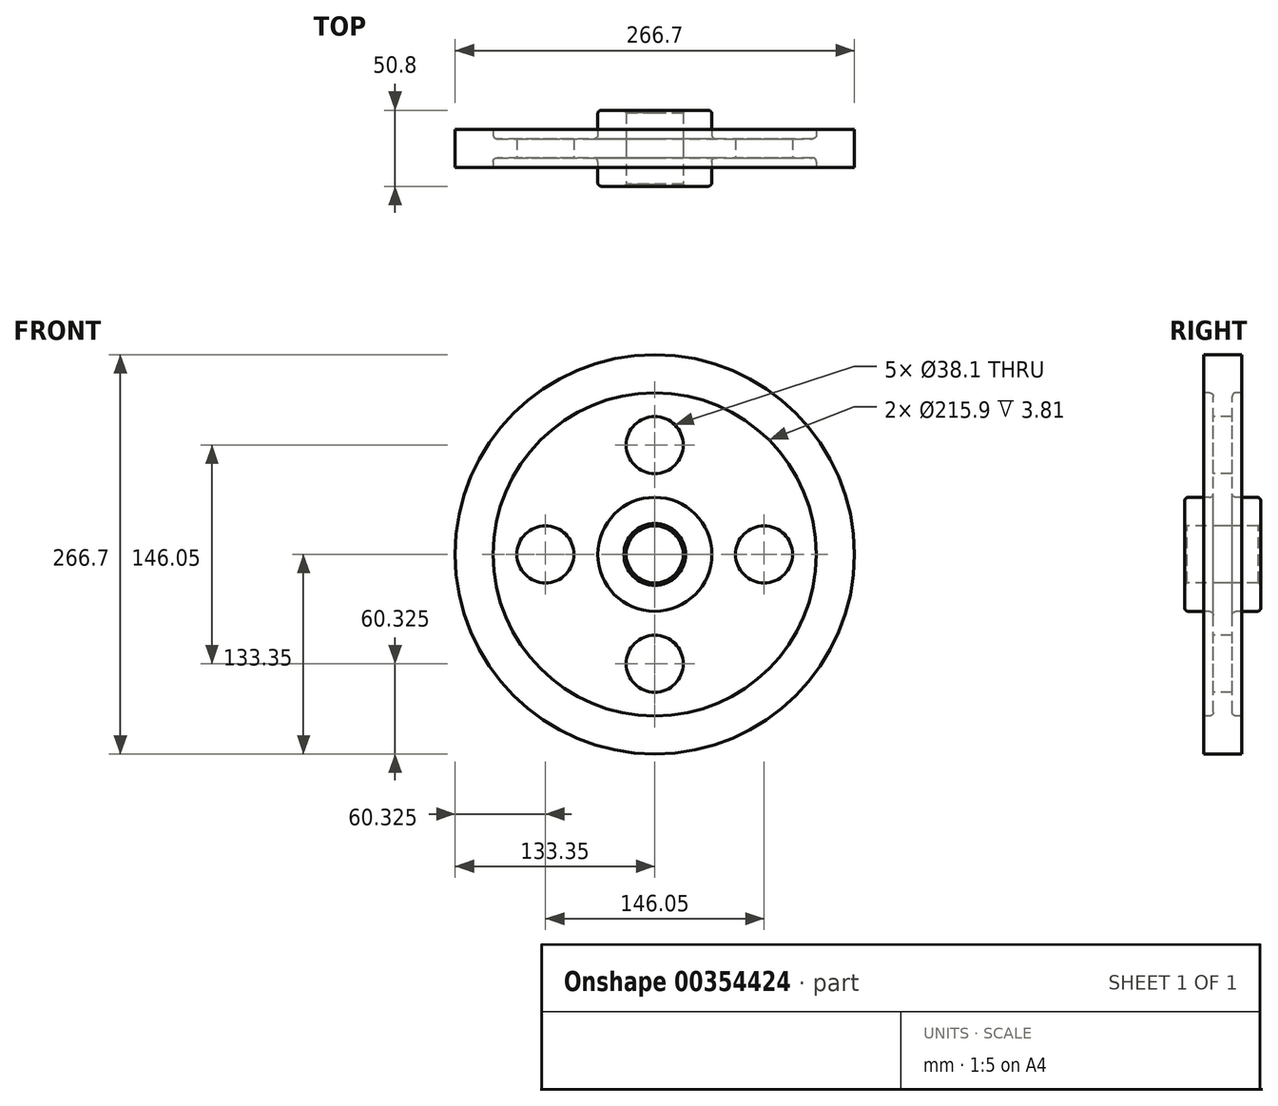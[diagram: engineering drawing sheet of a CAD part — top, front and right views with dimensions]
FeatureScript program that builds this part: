
annotation { "Feature Type Name" : "Feature", "Feature Type Description" : "" }
export const myFeature = defineFeature(function(context is Context, id is Id, definition is map)
    precondition{}
    {
        {
            var Q0;
            Q0=qCreatedBy(makeId("Right.planeOp"),FACE);
            var sketch = newSketch(context, id + "F0", { "sketchPlane" : qUnion([Q0])});
            skLineSegment(sketch, "E0", {"start": v(0, 0) * mm, "end": v(0, 28.58) * mm});
            skLineSegment(sketch, "E1", {"start": v(0, 28.58) * mm, "end": v(0, 73.03) * mm});
            skLineSegment(sketch, "E2", {"start": v(0, 73.03) * mm, "end": v(0, 120.65) * mm});
            skLineSegment(sketch, "E3.bottom", {"start": v(25.4, 19.05) * mm, "end": v(-25.4, 19.05) * mm});
            skLineSegment(sketch, "E3.top", {"start": v(25.4, 38.1) * mm, "end": v(6.35, 38.1) * mm});
            skLineSegment(sketch, "E3.left", {"start": v(25.4, 19.05) * mm, "end": v(25.4, 38.1) * mm});
            skLineSegment(sketch, "E3.right", {"start": v(-25.4, 19.05) * mm, "end": v(-25.4, 38.1) * mm});
            skPoint(sketch, "E3.middle", {"position": v(0, 28.58) * mm});
            skLineSegment(sketch, "E4.bottom", {"start": v(12.7, 133.35) * mm, "end": v(-12.7, 133.35) * mm});
            skLineSegment(sketch, "E4.top", {"start": v(12.7, 107.95) * mm, "end": v(6.35, 107.95) * mm});
            skLineSegment(sketch, "E4.left", {"start": v(12.7, 133.35) * mm, "end": v(12.7, 107.95) * mm});
            skLineSegment(sketch, "E4.right", {"start": v(-12.7, 133.35) * mm, "end": v(-12.7, 107.95) * mm});
            skPoint(sketch, "E4.middle", {"position": v(0, 120.65) * mm});
            skLineSegment(sketch, "E5.left", {"start": v(6.35, 32.76) * mm, "end": v(6.35, 113.29) * mm});
            skLineSegment(sketch, "E5.right", {"start": v(-6.35, 32.76) * mm, "end": v(-6.35, 113.29) * mm});
            skPoint(sketch, "E5.middle", {"position": v(0, 73.03) * mm});
            skLineSegment(sketch, "E6.trimOffspring", {"start": v(-6.35, 38.1) * mm, "end": v(-25.4, 38.1) * mm});
            skLineSegment(sketch, "E7.trimOffspring", {"start": v(-6.35, 107.95) * mm, "end": v(-12.7, 107.95) * mm});
            skLineSegment(sketch, "E8", {"start": v(0, 0) * mm, "end": v(75.64, 0) * mm});
            skLineSegment(sketch, "E9", {"start": v(0, 0) * mm, "end": v(32.48, 0) * mm});
            skSolve(sketch);
        }
        {
            var Q0;
            {var subQ4=sQuery(id+"F0.wireOp",EDGE,"E3.top");Q0=makeQuery(id+"F0.imprint","IMPRINT",FACE,{"disambiguationData":[TD([[makeQuery(id+"F0.imprint","IMPRINT",EDGE,{"derivedFrom":subQ4}),1.0]])]});}
            var Q1;
            Q1=sQuery(id+"F0.wireOp",EDGE,"E8");
            revolve(context, id + "F1", {"entities" : qUnion([Q0]), "axis" : qUnion([Q1]), "revolveType" : RevolveType.FULL});
        }
        {
            var Q0;
            Q0=makeQuery(id+"F1.opRevolve","SWEPT_FACE",FACE,{"disambiguationData":[OSD([sQuery(id+"F0.wireOp",EDGE,"E5.right")])]});
            var sketch = newSketch(context, id + "F2", { "sketchPlane" : qUnion([Q0])});
            skLineSegment(sketch, "E10", {"start": v(0, 0) * mm, "end": v(0, 73.03) * mm});
            skCircle(sketch, "E11", {"center": v(0, 73.03) * mm, "radius": 19.05 * mm});
            skCircle(sketch, "E12.1.0", {"center": v(-73.03, 0) * mm, "radius": 19.05 * mm});
            skCircle(sketch, "E12.2.0", {"center": v(0, -73.03) * mm, "radius": 19.05 * mm});
            skCircle(sketch, "E12.3.0", {"center": v(73.03, 0) * mm, "radius": 19.05 * mm});
            skPoint(sketch, "E12.center", {"position": v(0, 0) * mm});
            skSolve(sketch);
        }
        {
            var Q0;
            Q0=makeQuery(id+"F2.imprint","IMPRINT",FACE,{"disambiguationData":[TD([[makeQuery(id+"F2.imprint","IMPRINT",EDGE,{"derivedFrom":sQuery(id+"F2.wireOp",EDGE,"E12.1.0")}),1.0]])]});
            var Q1;
            Q1=makeQuery(id+"F2.imprint","IMPRINT",FACE,{"disambiguationData":[TD([[makeQuery(id+"F2.imprint","IMPRINT",EDGE,{"derivedFrom":sQuery(id+"F2.wireOp",EDGE,"E12.3.0")}),1.0]])]});
            var Q2;
            Q2=makeQuery(id+"F2.imprint","IMPRINT",FACE,{"disambiguationData":[TD([[makeQuery(id+"F2.imprint","IMPRINT",EDGE,{"derivedFrom":sQuery(id+"F2.wireOp",EDGE,"E12.2.0")}),1.0]])]});
            var Q3;
            Q3=makeQuery(id+"F2.imprint","IMPRINT",FACE,{"disambiguationData":[TD([[makeQuery(id+"F2.imprint","IMPRINT",EDGE,{"derivedFrom":sQuery(id+"F2.wireOp",EDGE,"E11")}),1.0]])]});
            extrude(context, id + "F3", {"entities" : qUnion([Q0, Q1, Q2, Q3]), "operationType" : NewBodyOperationType.REMOVE, "oppositeDirection" : true, "depth" : 25.4 * mm});
        }
        {
            var Q0;
            Q0=makeQuery(id+"F1.opRevolve","SWEPT_EDGE",EDGE,{"disambiguationData":[OSD([sQuery(id+"F0.wireOp",EDGE,"E3.right"),sQuery(id+"F0.wireOp",EDGE,"E6.trimOffspring")])]});
            var Q1;
            Q1=makeQuery(id+"F1.opRevolve","SWEPT_EDGE",EDGE,{"disambiguationData":[OSD([sQuery(id+"F0.wireOp",EDGE,"E5.right"),sQuery(id+"F0.wireOp",EDGE,"E6.trimOffspring")])]});
            var Q2;
            Q2=makeQuery(id+"F1.opRevolve","SWEPT_EDGE",EDGE,{"disambiguationData":[OSD([sQuery(id+"F0.wireOp",EDGE,"E5.right"),sQuery(id+"F0.wireOp",EDGE,"E7.trimOffspring")])]});
            var Q3;
            Q3=makeQuery(id+"F1.opRevolve","SWEPT_EDGE",EDGE,{"disambiguationData":[OSD([sQuery(id+"F0.wireOp",EDGE,"E3.top"),sQuery(id+"F0.wireOp",EDGE,"E3.left")])]});
            var Q4;
            Q4=makeQuery(id+"F1.opRevolve","SWEPT_EDGE",EDGE,{"disambiguationData":[OSD([sQuery(id+"F0.wireOp",EDGE,"E3.top"),sQuery(id+"F0.wireOp",EDGE,"E5.left")])]});
            var Q5;
            Q5=makeQuery(id+"F1.opRevolve","SWEPT_EDGE",EDGE,{"disambiguationData":[OSD([sQuery(id+"F0.wireOp",EDGE,"E4.top"),sQuery(id+"F0.wireOp",EDGE,"E5.left")])]});
            fillet(context, id + "F4", {"entities" : qUnion([Q0, Q1, Q2, Q3, Q4, Q5]), "radius" : 2.54 * mm, "tangentPropagation" : true, "allowEdgeOverflow" : false});
        }
        {
            var Q0;
            Q0=makeQuery(id+"F1.opRevolve","SWEPT_EDGE",EDGE,{"disambiguationData":[OSD([sQuery(id+"F0.wireOp",EDGE,"E3.bottom"),sQuery(id+"F0.wireOp",EDGE,"E3.right")])]});
            var Q1;
            Q1=makeQuery(id+"F1.opRevolve","SWEPT_EDGE",EDGE,{"disambiguationData":[OSD([sQuery(id+"F0.wireOp",EDGE,"E3.bottom"),sQuery(id+"F0.wireOp",EDGE,"E3.left")])]});
            chamfer(context, id + "F5", {"entities" : qUnion([Q0, Q1]), "width" : 1.59 * mm, "tangentPropagation" : true});
        }
    });
